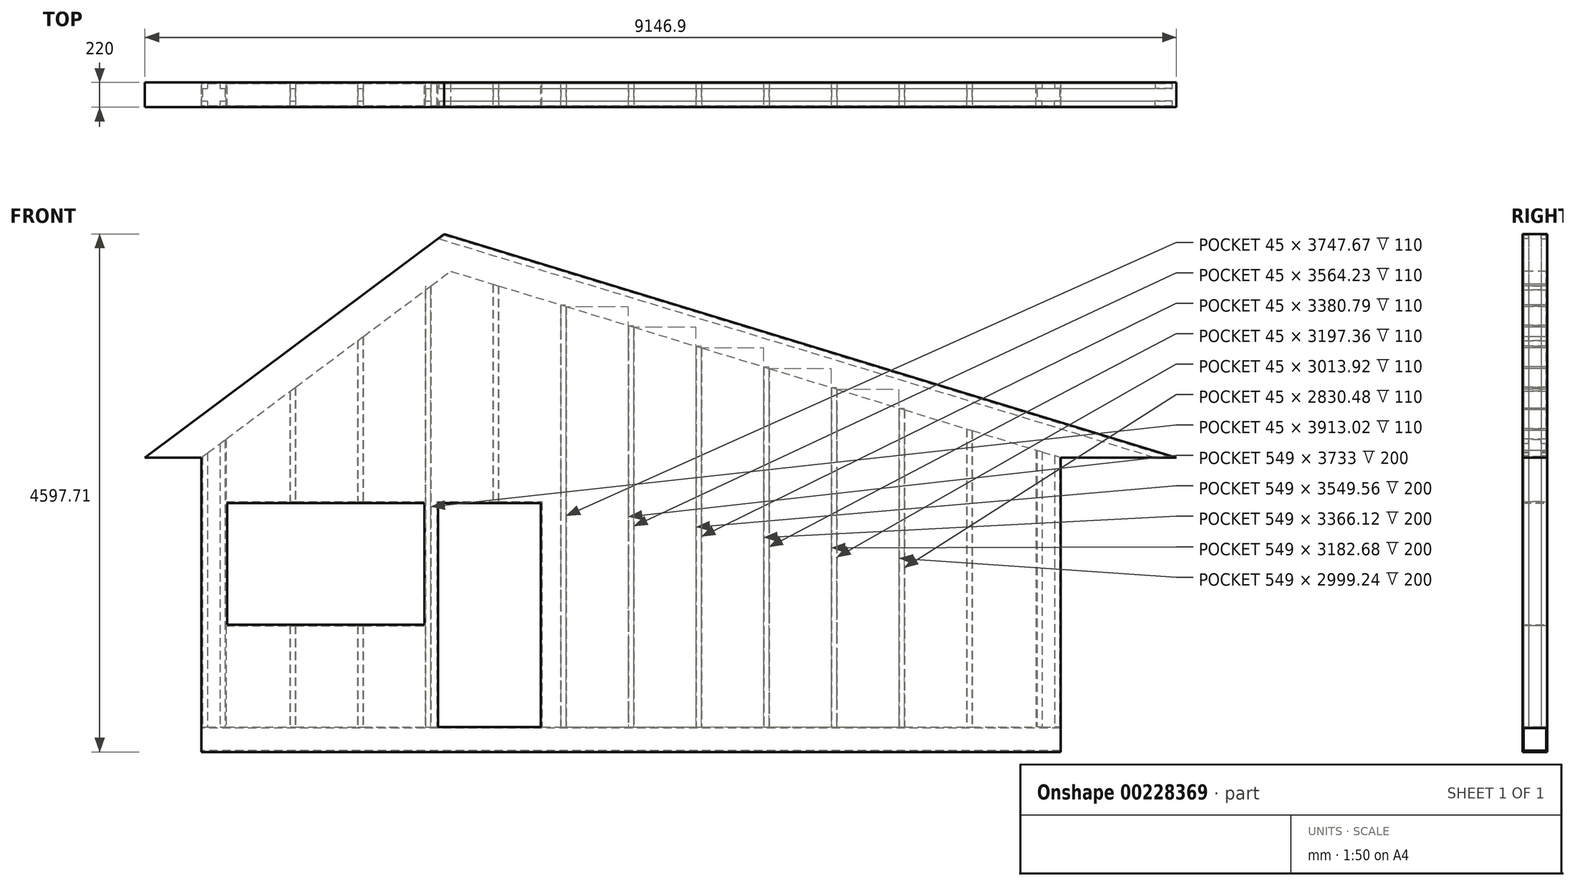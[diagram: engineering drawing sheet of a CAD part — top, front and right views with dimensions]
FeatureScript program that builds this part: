
annotation { "Feature Type Name" : "Feature", "Feature Type Description" : "" }
export const myFeature = defineFeature(function(context is Context, id is Id, definition is map)
    precondition{}
    {
        {
            var Q0;
            Q0=qCreatedBy(makeId("Top.planeOp"),FACE);
            var sketch = newSketch(context, id + "F0", { "sketchPlane" : qUnion([Q0])});
            skLineSegment(sketch, "E0.bottom", {"start": v(0, 0) * mm, "end": v(7600, 0) * mm});
            skLineSegment(sketch, "E0.top", {"start": v(0, -200) * mm, "end": v(7600, -200) * mm});
            skLineSegment(sketch, "E0.left", {"start": v(0, 0) * mm, "end": v(0, -200) * mm});
            skLineSegment(sketch, "E0.right", {"start": v(7600, 0) * mm, "end": v(7600, -200) * mm});
            skLineSegment(sketch, "E1.bottom", {"start": v(-10, 10) * mm, "end": v(7610, 10) * mm});
            skLineSegment(sketch, "E1.top", {"start": v(-10, -210) * mm, "end": v(7610, -210) * mm});
            skLineSegment(sketch, "E1.left", {"start": v(-10, 10) * mm, "end": v(-10, -210) * mm});
            skLineSegment(sketch, "E1.right", {"start": v(7610, 10) * mm, "end": v(7610, -210) * mm});
            skLineSegment(sketch, "E2.bottom", {"start": v(0, 0) * mm, "end": v(45, 0) * mm});
            skLineSegment(sketch, "E2.top", {"start": v(0, -45) * mm, "end": v(45, -45) * mm});
            skLineSegment(sketch, "E2.left", {"start": v(0, 0) * mm, "end": v(0, -45) * mm});
            skLineSegment(sketch, "E2.right", {"start": v(45, 0) * mm, "end": v(45, -45) * mm});
            skLineSegment(sketch, "E3.0.1.0", {"start": v(0, -200) * mm, "end": v(45, -200) * mm});
            skLineSegment(sketch, "E3.0.1.1", {"start": v(0, -155) * mm, "end": v(0, -200) * mm});
            skLineSegment(sketch, "E3.0.1.2", {"start": v(0, -155) * mm, "end": v(45, -155) * mm});
            skLineSegment(sketch, "E3.0.1.3", {"start": v(45, -155) * mm, "end": v(45, -200) * mm});
            skLineSegment(sketch, "E3.1.0.0", {"start": v(155, -45) * mm, "end": v(200, -45) * mm});
            skLineSegment(sketch, "E3.1.0.1", {"start": v(155, 0) * mm, "end": v(155, -45) * mm});
            skLineSegment(sketch, "E3.1.0.2", {"start": v(155, 0) * mm, "end": v(200, 0) * mm});
            skLineSegment(sketch, "E3.1.0.3", {"start": v(200, 0) * mm, "end": v(200, -45) * mm});
            skLineSegment(sketch, "E3.1.1.0", {"start": v(155, -200) * mm, "end": v(200, -200) * mm});
            skLineSegment(sketch, "E3.1.1.1", {"start": v(155, -155) * mm, "end": v(155, -200) * mm});
            skLineSegment(sketch, "E3.1.1.2", {"start": v(155, -155) * mm, "end": v(200, -155) * mm});
            skLineSegment(sketch, "E3.1.1.3", {"start": v(200, -155) * mm, "end": v(200, -200) * mm});
            skLineSegment(sketch, "E3.direction1", {"start": v(0, -45) * mm, "end": v(155, -45) * mm, "construction": true});
            skLineSegment(sketch, "E3.direction2", {"start": v(0, -45) * mm, "end": v(0, -200) * mm, "construction": true});
            skLineSegment(sketch, "E4", {"start": v(200, 0) * mm, "end": v(200, -200) * mm});
            skLineSegment(sketch, "E5", {"start": v(210, 0) * mm, "end": v(210, -200) * mm});
            skLineSegment(sketch, "E6.bottom", {"start": v(777.5, 0) * mm, "end": v(822.5, 0) * mm});
            skLineSegment(sketch, "E6.top", {"start": v(777.5, -45) * mm, "end": v(822.5, -45) * mm});
            skLineSegment(sketch, "E6.left", {"start": v(777.5, 0) * mm, "end": v(777.5, -45) * mm});
            skLineSegment(sketch, "E6.right", {"start": v(822.5, 0) * mm, "end": v(822.5, -45) * mm});
            skLineSegment(sketch, "E7.bottom", {"start": v(777.5, -200) * mm, "end": v(822.5, -200) * mm});
            skLineSegment(sketch, "E7.top", {"start": v(777.5, -155) * mm, "end": v(822.5, -155) * mm});
            skLineSegment(sketch, "E7.left", {"start": v(777.5, -200) * mm, "end": v(777.5, -155) * mm});
            skLineSegment(sketch, "E7.right", {"start": v(822.5, -200) * mm, "end": v(822.5, -155) * mm});
            skLineSegment(sketch, "E8", {"start": v(774.5, 0) * mm, "end": v(774.5, -200) * mm});
            skLineSegment(sketch, "E9", {"start": v(777.5, -45) * mm, "end": v(777.5, -155) * mm});
            skLineSegment(sketch, "E10", {"start": v(822.5, -45) * mm, "end": v(822.5, -155) * mm});
            skLineSegment(sketch, "E11", {"start": v(825.5, 0) * mm, "end": v(825.5, -200) * mm});
            skLineSegment(sketch, "E12", {"start": v(800, -200) * mm, "end": v(800, -155) * mm});
            skLineSegment(sketch, "E13.1.0.0", {"start": v(1400, -200) * mm, "end": v(1400, -155) * mm});
            skLineSegment(sketch, "E13.1.0.1", {"start": v(1377.5, -200) * mm, "end": v(1377.5, -155) * mm});
            skLineSegment(sketch, "E13.1.0.2", {"start": v(1374.5, 0) * mm, "end": v(1374.5, -200) * mm});
            skLineSegment(sketch, "E13.1.0.3", {"start": v(1377.5, -45) * mm, "end": v(1422.5, -45) * mm});
            skLineSegment(sketch, "E13.1.0.4", {"start": v(1377.5, -155) * mm, "end": v(1422.5, -155) * mm});
            skLineSegment(sketch, "E13.1.0.5", {"start": v(1377.5, -200) * mm, "end": v(1422.5, -200) * mm});
            skLineSegment(sketch, "E13.1.0.6", {"start": v(1377.5, 0) * mm, "end": v(1377.5, -45) * mm});
            skLineSegment(sketch, "E13.1.0.7", {"start": v(1422.5, -45) * mm, "end": v(1422.5, -155) * mm});
            skLineSegment(sketch, "E13.1.0.8", {"start": v(1377.5, -45) * mm, "end": v(1377.5, -155) * mm});
            skLineSegment(sketch, "E13.1.0.9", {"start": v(1422.5, -200) * mm, "end": v(1422.5, -155) * mm});
            skLineSegment(sketch, "E13.1.0.10", {"start": v(1377.5, 0) * mm, "end": v(1422.5, 0) * mm});
            skLineSegment(sketch, "E13.1.0.11", {"start": v(1422.5, 0) * mm, "end": v(1422.5, -45) * mm});
            skLineSegment(sketch, "E13.1.0.12", {"start": v(1425.5, 0) * mm, "end": v(1425.5, -200) * mm});
            skLineSegment(sketch, "E13.2.0.0", {"start": v(2000, -200) * mm, "end": v(2000, -155) * mm});
            skLineSegment(sketch, "E13.2.0.1", {"start": v(1977.5, -200) * mm, "end": v(1977.5, -155) * mm});
            skLineSegment(sketch, "E13.2.0.2", {"start": v(1974.5, 0) * mm, "end": v(1974.5, -200) * mm});
            skLineSegment(sketch, "E13.2.0.3", {"start": v(1977.5, -45) * mm, "end": v(2022.5, -45) * mm});
            skLineSegment(sketch, "E13.2.0.4", {"start": v(1977.5, -155) * mm, "end": v(2022.5, -155) * mm});
            skLineSegment(sketch, "E13.2.0.5", {"start": v(1977.5, -200) * mm, "end": v(2022.5, -200) * mm});
            skLineSegment(sketch, "E13.2.0.6", {"start": v(1977.5, 0) * mm, "end": v(1977.5, -45) * mm});
            skLineSegment(sketch, "E13.2.0.7", {"start": v(2022.5, -45) * mm, "end": v(2022.5, -155) * mm});
            skLineSegment(sketch, "E13.2.0.8", {"start": v(1977.5, -45) * mm, "end": v(1977.5, -155) * mm});
            skLineSegment(sketch, "E13.2.0.9", {"start": v(2022.5, -200) * mm, "end": v(2022.5, -155) * mm});
            skLineSegment(sketch, "E13.2.0.10", {"start": v(1977.5, 0) * mm, "end": v(2022.5, 0) * mm});
            skLineSegment(sketch, "E13.2.0.11", {"start": v(2022.5, 0) * mm, "end": v(2022.5, -45) * mm});
            skLineSegment(sketch, "E13.2.0.12", {"start": v(2025.5, 0) * mm, "end": v(2025.5, -200) * mm});
            skLineSegment(sketch, "E13.3.0.0", {"start": v(2600, -200) * mm, "end": v(2600, -155) * mm});
            skLineSegment(sketch, "E13.3.0.1", {"start": v(2577.5, -200) * mm, "end": v(2577.5, -155) * mm});
            skLineSegment(sketch, "E13.3.0.2", {"start": v(2574.5, 0) * mm, "end": v(2574.5, -200) * mm});
            skLineSegment(sketch, "E13.3.0.3", {"start": v(2577.5, -45) * mm, "end": v(2622.5, -45) * mm});
            skLineSegment(sketch, "E13.3.0.4", {"start": v(2577.5, -155) * mm, "end": v(2622.5, -155) * mm});
            skLineSegment(sketch, "E13.3.0.5", {"start": v(2577.5, -200) * mm, "end": v(2622.5, -200) * mm});
            skLineSegment(sketch, "E13.3.0.6", {"start": v(2577.5, 0) * mm, "end": v(2577.5, -45) * mm});
            skLineSegment(sketch, "E13.3.0.7", {"start": v(2622.5, -45) * mm, "end": v(2622.5, -155) * mm});
            skLineSegment(sketch, "E13.3.0.8", {"start": v(2577.5, -45) * mm, "end": v(2577.5, -155) * mm});
            skLineSegment(sketch, "E13.3.0.9", {"start": v(2622.5, -200) * mm, "end": v(2622.5, -155) * mm});
            skLineSegment(sketch, "E13.3.0.10", {"start": v(2577.5, 0) * mm, "end": v(2622.5, 0) * mm});
            skLineSegment(sketch, "E13.3.0.11", {"start": v(2622.5, 0) * mm, "end": v(2622.5, -45) * mm});
            skLineSegment(sketch, "E13.3.0.12", {"start": v(2625.5, 0) * mm, "end": v(2625.5, -200) * mm});
            skLineSegment(sketch, "E13.4.0.0", {"start": v(3200, -200) * mm, "end": v(3200, -155) * mm});
            skLineSegment(sketch, "E13.4.0.1", {"start": v(3177.5, -200) * mm, "end": v(3177.5, -155) * mm});
            skLineSegment(sketch, "E13.4.0.2", {"start": v(3174.5, 0) * mm, "end": v(3174.5, -200) * mm});
            skLineSegment(sketch, "E13.4.0.3", {"start": v(3177.5, -45) * mm, "end": v(3222.5, -45) * mm});
            skLineSegment(sketch, "E13.4.0.4", {"start": v(3177.5, -155) * mm, "end": v(3222.5, -155) * mm});
            skLineSegment(sketch, "E13.4.0.5", {"start": v(3177.5, -200) * mm, "end": v(3222.5, -200) * mm});
            skLineSegment(sketch, "E13.4.0.6", {"start": v(3177.5, 0) * mm, "end": v(3177.5, -45) * mm});
            skLineSegment(sketch, "E13.4.0.7", {"start": v(3222.5, -45) * mm, "end": v(3222.5, -155) * mm});
            skLineSegment(sketch, "E13.4.0.8", {"start": v(3177.5, -45) * mm, "end": v(3177.5, -155) * mm});
            skLineSegment(sketch, "E13.4.0.9", {"start": v(3222.5, -200) * mm, "end": v(3222.5, -155) * mm});
            skLineSegment(sketch, "E13.4.0.10", {"start": v(3177.5, 0) * mm, "end": v(3222.5, 0) * mm});
            skLineSegment(sketch, "E13.4.0.11", {"start": v(3222.5, 0) * mm, "end": v(3222.5, -45) * mm});
            skLineSegment(sketch, "E13.4.0.12", {"start": v(3225.5, 0) * mm, "end": v(3225.5, -200) * mm});
            skLineSegment(sketch, "E13.5.0.0", {"start": v(3800, -200) * mm, "end": v(3800, -155) * mm});
            skLineSegment(sketch, "E13.5.0.1", {"start": v(3777.5, -200) * mm, "end": v(3777.5, -155) * mm});
            skLineSegment(sketch, "E13.5.0.2", {"start": v(3774.5, 0) * mm, "end": v(3774.5, -200) * mm});
            skLineSegment(sketch, "E13.5.0.3", {"start": v(3777.5, -45) * mm, "end": v(3822.5, -45) * mm});
            skLineSegment(sketch, "E13.5.0.4", {"start": v(3777.5, -155) * mm, "end": v(3822.5, -155) * mm});
            skLineSegment(sketch, "E13.5.0.5", {"start": v(3777.5, -200) * mm, "end": v(3822.5, -200) * mm});
            skLineSegment(sketch, "E13.5.0.6", {"start": v(3777.5, 0) * mm, "end": v(3777.5, -45) * mm});
            skLineSegment(sketch, "E13.5.0.7", {"start": v(3822.5, -45) * mm, "end": v(3822.5, -155) * mm});
            skLineSegment(sketch, "E13.5.0.8", {"start": v(3777.5, -45) * mm, "end": v(3777.5, -155) * mm});
            skLineSegment(sketch, "E13.5.0.9", {"start": v(3822.5, -200) * mm, "end": v(3822.5, -155) * mm});
            skLineSegment(sketch, "E13.5.0.10", {"start": v(3777.5, 0) * mm, "end": v(3822.5, 0) * mm});
            skLineSegment(sketch, "E13.5.0.11", {"start": v(3822.5, 0) * mm, "end": v(3822.5, -45) * mm});
            skLineSegment(sketch, "E13.5.0.12", {"start": v(3825.5, 0) * mm, "end": v(3825.5, -200) * mm});
            skLineSegment(sketch, "E13.6.0.0", {"start": v(4400, -200) * mm, "end": v(4400, -155) * mm});
            skLineSegment(sketch, "E13.6.0.1", {"start": v(4377.5, -200) * mm, "end": v(4377.5, -155) * mm});
            skLineSegment(sketch, "E13.6.0.2", {"start": v(4374.5, 0) * mm, "end": v(4374.5, -200) * mm});
            skLineSegment(sketch, "E13.6.0.3", {"start": v(4377.5, -45) * mm, "end": v(4422.5, -45) * mm});
            skLineSegment(sketch, "E13.6.0.4", {"start": v(4377.5, -155) * mm, "end": v(4422.5, -155) * mm});
            skLineSegment(sketch, "E13.6.0.5", {"start": v(4377.5, -200) * mm, "end": v(4422.5, -200) * mm});
            skLineSegment(sketch, "E13.6.0.6", {"start": v(4377.5, 0) * mm, "end": v(4377.5, -45) * mm});
            skLineSegment(sketch, "E13.6.0.7", {"start": v(4422.5, -45) * mm, "end": v(4422.5, -155) * mm});
            skLineSegment(sketch, "E13.6.0.8", {"start": v(4377.5, -45) * mm, "end": v(4377.5, -155) * mm});
            skLineSegment(sketch, "E13.6.0.9", {"start": v(4422.5, -200) * mm, "end": v(4422.5, -155) * mm});
            skLineSegment(sketch, "E13.6.0.10", {"start": v(4377.5, 0) * mm, "end": v(4422.5, 0) * mm});
            skLineSegment(sketch, "E13.6.0.11", {"start": v(4422.5, 0) * mm, "end": v(4422.5, -45) * mm});
            skLineSegment(sketch, "E13.6.0.12", {"start": v(4425.5, 0) * mm, "end": v(4425.5, -200) * mm});
            skLineSegment(sketch, "E13.7.0.0", {"start": v(5000, -200) * mm, "end": v(5000, -155) * mm});
            skLineSegment(sketch, "E13.7.0.1", {"start": v(4977.5, -200) * mm, "end": v(4977.5, -155) * mm});
            skLineSegment(sketch, "E13.7.0.2", {"start": v(4974.5, 0) * mm, "end": v(4974.5, -200) * mm});
            skLineSegment(sketch, "E13.7.0.3", {"start": v(4977.5, -45) * mm, "end": v(5022.5, -45) * mm});
            skLineSegment(sketch, "E13.7.0.4", {"start": v(4977.5, -155) * mm, "end": v(5022.5, -155) * mm});
            skLineSegment(sketch, "E13.7.0.5", {"start": v(4977.5, -200) * mm, "end": v(5022.5, -200) * mm});
            skLineSegment(sketch, "E13.7.0.6", {"start": v(4977.5, 0) * mm, "end": v(4977.5, -45) * mm});
            skLineSegment(sketch, "E13.7.0.7", {"start": v(5022.5, -45) * mm, "end": v(5022.5, -155) * mm});
            skLineSegment(sketch, "E13.7.0.8", {"start": v(4977.5, -45) * mm, "end": v(4977.5, -155) * mm});
            skLineSegment(sketch, "E13.7.0.9", {"start": v(5022.5, -200) * mm, "end": v(5022.5, -155) * mm});
            skLineSegment(sketch, "E13.7.0.10", {"start": v(4977.5, 0) * mm, "end": v(5022.5, 0) * mm});
            skLineSegment(sketch, "E13.7.0.11", {"start": v(5022.5, 0) * mm, "end": v(5022.5, -45) * mm});
            skLineSegment(sketch, "E13.7.0.12", {"start": v(5025.5, 0) * mm, "end": v(5025.5, -200) * mm});
            skLineSegment(sketch, "E13.8.0.0", {"start": v(5600, -200) * mm, "end": v(5600, -155) * mm});
            skLineSegment(sketch, "E13.8.0.1", {"start": v(5577.5, -200) * mm, "end": v(5577.5, -155) * mm});
            skLineSegment(sketch, "E13.8.0.2", {"start": v(5574.5, 0) * mm, "end": v(5574.5, -200) * mm});
            skLineSegment(sketch, "E13.8.0.3", {"start": v(5577.5, -45) * mm, "end": v(5622.5, -45) * mm});
            skLineSegment(sketch, "E13.8.0.4", {"start": v(5577.5, -155) * mm, "end": v(5622.5, -155) * mm});
            skLineSegment(sketch, "E13.8.0.5", {"start": v(5577.5, -200) * mm, "end": v(5622.5, -200) * mm});
            skLineSegment(sketch, "E13.8.0.6", {"start": v(5577.5, 0) * mm, "end": v(5577.5, -45) * mm});
            skLineSegment(sketch, "E13.8.0.7", {"start": v(5622.5, -45) * mm, "end": v(5622.5, -155) * mm});
            skLineSegment(sketch, "E13.8.0.8", {"start": v(5577.5, -45) * mm, "end": v(5577.5, -155) * mm});
            skLineSegment(sketch, "E13.8.0.9", {"start": v(5622.5, -200) * mm, "end": v(5622.5, -155) * mm});
            skLineSegment(sketch, "E13.8.0.10", {"start": v(5577.5, 0) * mm, "end": v(5622.5, 0) * mm});
            skLineSegment(sketch, "E13.8.0.11", {"start": v(5622.5, 0) * mm, "end": v(5622.5, -45) * mm});
            skLineSegment(sketch, "E13.8.0.12", {"start": v(5625.5, 0) * mm, "end": v(5625.5, -200) * mm});
            skLineSegment(sketch, "E13.9.0.0", {"start": v(6200, -200) * mm, "end": v(6200, -155) * mm});
            skLineSegment(sketch, "E13.9.0.1", {"start": v(6177.5, -200) * mm, "end": v(6177.5, -155) * mm});
            skLineSegment(sketch, "E13.9.0.2", {"start": v(6174.5, 0) * mm, "end": v(6174.5, -200) * mm});
            skLineSegment(sketch, "E13.9.0.3", {"start": v(6177.5, -45) * mm, "end": v(6222.5, -45) * mm});
            skLineSegment(sketch, "E13.9.0.4", {"start": v(6177.5, -155) * mm, "end": v(6222.5, -155) * mm});
            skLineSegment(sketch, "E13.9.0.5", {"start": v(6177.5, -200) * mm, "end": v(6222.5, -200) * mm});
            skLineSegment(sketch, "E13.9.0.6", {"start": v(6177.5, 0) * mm, "end": v(6177.5, -45) * mm});
            skLineSegment(sketch, "E13.9.0.7", {"start": v(6222.5, -45) * mm, "end": v(6222.5, -155) * mm});
            skLineSegment(sketch, "E13.9.0.8", {"start": v(6177.5, -45) * mm, "end": v(6177.5, -155) * mm});
            skLineSegment(sketch, "E13.9.0.9", {"start": v(6222.5, -200) * mm, "end": v(6222.5, -155) * mm});
            skLineSegment(sketch, "E13.9.0.10", {"start": v(6177.5, 0) * mm, "end": v(6222.5, 0) * mm});
            skLineSegment(sketch, "E13.9.0.11", {"start": v(6222.5, 0) * mm, "end": v(6222.5, -45) * mm});
            skLineSegment(sketch, "E13.9.0.12", {"start": v(6225.5, 0) * mm, "end": v(6225.5, -200) * mm});
            skLineSegment(sketch, "E13.10.0.0", {"start": v(6800, -200) * mm, "end": v(6800, -155) * mm});
            skLineSegment(sketch, "E13.10.0.1", {"start": v(6777.5, -200) * mm, "end": v(6777.5, -155) * mm});
            skLineSegment(sketch, "E13.10.0.2", {"start": v(6774.5, 0) * mm, "end": v(6774.5, -200) * mm});
            skLineSegment(sketch, "E13.10.0.3", {"start": v(6777.5, -45) * mm, "end": v(6822.5, -45) * mm});
            skLineSegment(sketch, "E13.10.0.4", {"start": v(6777.5, -155) * mm, "end": v(6822.5, -155) * mm});
            skLineSegment(sketch, "E13.10.0.5", {"start": v(6777.5, -200) * mm, "end": v(6822.5, -200) * mm});
            skLineSegment(sketch, "E13.10.0.6", {"start": v(6777.5, 0) * mm, "end": v(6777.5, -45) * mm});
            skLineSegment(sketch, "E13.10.0.7", {"start": v(6822.5, -45) * mm, "end": v(6822.5, -155) * mm});
            skLineSegment(sketch, "E13.10.0.8", {"start": v(6777.5, -45) * mm, "end": v(6777.5, -155) * mm});
            skLineSegment(sketch, "E13.10.0.9", {"start": v(6822.5, -200) * mm, "end": v(6822.5, -155) * mm});
            skLineSegment(sketch, "E13.10.0.10", {"start": v(6777.5, 0) * mm, "end": v(6822.5, 0) * mm});
            skLineSegment(sketch, "E13.10.0.11", {"start": v(6822.5, 0) * mm, "end": v(6822.5, -45) * mm});
            skLineSegment(sketch, "E13.10.0.12", {"start": v(6825.5, 0) * mm, "end": v(6825.5, -200) * mm});
            skLineSegment(sketch, "E13.direction1", {"start": v(777.5, -155) * mm, "end": v(1377.5, -155) * mm, "construction": true});
            skLineSegment(sketch, "E14.bottom", {"start": v(7600, 0) * mm, "end": v(7556, 0) * mm});
            skLineSegment(sketch, "E14.top", {"start": v(7600, -45) * mm, "end": v(7556, -45) * mm});
            skLineSegment(sketch, "E14.left", {"start": v(7600, 0) * mm, "end": v(7600, -45) * mm});
            skLineSegment(sketch, "E14.right", {"start": v(7556, 0) * mm, "end": v(7556, -45) * mm});
            skLineSegment(sketch, "E15.bottom", {"start": v(7600, -200) * mm, "end": v(7555, -200) * mm});
            skLineSegment(sketch, "E15.top", {"start": v(7600, -155) * mm, "end": v(7555, -155) * mm});
            skLineSegment(sketch, "E15.left", {"start": v(7600, -200) * mm, "end": v(7600, -155) * mm});
            skLineSegment(sketch, "E15.right", {"start": v(7555, -200) * mm, "end": v(7555, -155) * mm});
            skLineSegment(sketch, "E16.bottom", {"start": v(7445, -200) * mm, "end": v(7400, -200) * mm});
            skLineSegment(sketch, "E16.top", {"start": v(7445, -155) * mm, "end": v(7400, -155) * mm});
            skLineSegment(sketch, "E16.left", {"start": v(7445, -200) * mm, "end": v(7445, -155) * mm});
            skLineSegment(sketch, "E16.right", {"start": v(7400, -200) * mm, "end": v(7400, -155) * mm});
            skLineSegment(sketch, "E17.bottom", {"start": v(7445, 0) * mm, "end": v(7400, 0) * mm});
            skLineSegment(sketch, "E17.top", {"start": v(7445, -45) * mm, "end": v(7400, -45) * mm});
            skLineSegment(sketch, "E17.left", {"start": v(7445, 0) * mm, "end": v(7445, -45) * mm});
            skLineSegment(sketch, "E17.right", {"start": v(7400, 0) * mm, "end": v(7400, -45) * mm});
            skLineSegment(sketch, "E18", {"start": v(7400, -45) * mm, "end": v(7400, -155) * mm});
            skLineSegment(sketch, "E19", {"start": v(7390, -200) * mm, "end": v(7390, 0) * mm});
            skSolve(sketch);
        }
        {
            var Q0;
            Q0 = qSketchRegion(id + "F0", true);
            var Q1;
            {var subQ4=sQuery(id+"F0.wireOp",EDGE,"E2.top");Q1=makeQuery(id+"F0.imprint","IMPRINT",FACE,{"disambiguationData":[TD([[makeQuery(id+"F0.imprint","IMPRINT",EDGE,{"derivedFrom":subQ4}),1.0]])]});}
            var Q2;
            {var subQ4=sQuery(id+"F0.wireOp",EDGE,"E3.0.1.2");Q2=makeQuery(id+"F0.imprint","IMPRINT",FACE,{"disambiguationData":[TD([[makeQuery(id+"F0.imprint","IMPRINT",EDGE,{"derivedFrom":subQ4}),-1.0]])]});}
            var Q3;
            {var subQ0=sQuery(id+"F0.wireOp",EDGE,"E3.1.1.1");Q3=makeQuery(id+"F0.imprint","IMPRINT",FACE,{"disambiguationData":[TD([[makeQuery(id+"F0.imprint","IMPRINT",EDGE,{"derivedFrom":subQ0}),1.0]])]});}
            var Q4;
            Q4=makeQuery(id+"F0.imprint","IMPRINT",FACE,{"disambiguationData":[TD([[makeQuery(id+"F0.imprint","IMPRINT",EDGE,{"derivedFrom":sQuery(id+"F0.wireOp",EDGE,"E3.1.0.0")}),1.0]])]});
            var Q5;
            {var subQ1=sQuery(id+"F0.wireOp",EDGE,"E3.1.0.3");Q5=makeQuery(id+"F0.imprint","IMPRINT",FACE,{"disambiguationData":[TD([[makeQuery(id+"F0.imprint","IMPRINT",EDGE,{"derivedFrom":subQ1}),1.0]])]});}
            var Q6;
            Q6=makeQuery(id+"F0.imprint","IMPRINT",FACE,{"disambiguationData":[TD([[makeQuery(id+"F0.imprint","IMPRINT",EDGE,{"derivedFrom":sQuery(id+"F0.wireOp",EDGE,"E6.top")}),1.0]])]});
            var Q7;
            {var subQ3=sQuery(id+"F0.wireOp",EDGE,"E6.left");Q7=makeQuery(id+"F0.imprint","IMPRINT",FACE,{"disambiguationData":[TD([[makeQuery(id+"F0.imprint","IMPRINT",EDGE,{"derivedFrom":subQ3}),-1.0]])]});}
            var Q8;
            {var subQ0=sQuery(id+"F0.wireOp",EDGE,"E6.right");Q8=makeQuery(id+"F0.imprint","IMPRINT",FACE,{"disambiguationData":[TD([[makeQuery(id+"F0.imprint","IMPRINT",EDGE,{"derivedFrom":subQ0}),1.0]])]});}
            var Q9;
            {var subQ0=sQuery(id+"F0.wireOp",EDGE,"E7.right");Q9=makeQuery(id+"F0.imprint","IMPRINT",FACE,{"disambiguationData":[TD([[makeQuery(id+"F0.imprint","IMPRINT",EDGE,{"derivedFrom":subQ0}),1.0]])]});}
            var Q10;
            {var subQ0=sQuery(id+"F0.wireOp",EDGE,"E7.left");Q10=makeQuery(id+"F0.imprint","IMPRINT",FACE,{"disambiguationData":[TD([[makeQuery(id+"F0.imprint","IMPRINT",EDGE,{"derivedFrom":subQ0}),-1.0]])]});}
            var Q11;
            Q11=makeQuery(id+"F0.imprint","IMPRINT",FACE,{"disambiguationData":[TD([[makeQuery(id+"F0.imprint","IMPRINT",EDGE,{"derivedFrom":sQuery(id+"F0.wireOp",EDGE,"E13.1.0.3")}),1.0]])]});
            var Q12;
            {var subQ0=sQuery(id+"F0.wireOp",EDGE,"E13.1.0.1");Q12=makeQuery(id+"F0.imprint","IMPRINT",FACE,{"disambiguationData":[TD([[makeQuery(id+"F0.imprint","IMPRINT",EDGE,{"derivedFrom":subQ0}),1.0]])]});}
            var Q13;
            Q13=makeQuery(id+"F0.imprint","IMPRINT",FACE,{"disambiguationData":[TD([[makeQuery(id+"F0.imprint","IMPRINT",EDGE,{"derivedFrom":sQuery(id+"F0.wireOp",EDGE,"E13.1.0.7")}),1.0]])]});
            var Q14;
            {var subQ0=sQuery(id+"F0.wireOp",EDGE,"E13.1.0.0");Q14=makeQuery(id+"F0.imprint","IMPRINT",FACE,{"disambiguationData":[TD([[makeQuery(id+"F0.imprint","IMPRINT",EDGE,{"derivedFrom":subQ0}),-1.0]])]});}
            var Q15;
            {var subQ0=sQuery(id+"F0.wireOp",EDGE,"E13.1.0.0");Q15=makeQuery(id+"F0.imprint","IMPRINT",FACE,{"disambiguationData":[TD([[makeQuery(id+"F0.imprint","IMPRINT",EDGE,{"derivedFrom":subQ0}),1.0]])]});}
            var Q16;
            Q16=makeQuery(id+"F0.imprint","IMPRINT",FACE,{"disambiguationData":[TD([[makeQuery(id+"F0.imprint","IMPRINT",EDGE,{"derivedFrom":sQuery(id+"F0.wireOp",EDGE,"E13.2.0.3")}),1.0]])]});
            var Q17;
            {var subQ0=sQuery(id+"F0.wireOp",EDGE,"E13.2.0.0");Q17=makeQuery(id+"F0.imprint","IMPRINT",FACE,{"disambiguationData":[TD([[makeQuery(id+"F0.imprint","IMPRINT",EDGE,{"derivedFrom":subQ0}),-1.0]])]});}
            var Q18;
            {var subQ0=sQuery(id+"F0.wireOp",EDGE,"E13.2.0.0");Q18=makeQuery(id+"F0.imprint","IMPRINT",FACE,{"disambiguationData":[TD([[makeQuery(id+"F0.imprint","IMPRINT",EDGE,{"derivedFrom":subQ0}),1.0]])]});}
            var Q19;
            {var subQ1=sQuery(id+"F0.wireOp",EDGE,"E13.2.0.1");Q19=makeQuery(id+"F0.imprint","IMPRINT",FACE,{"disambiguationData":[TD([[makeQuery(id+"F0.imprint","IMPRINT",EDGE,{"derivedFrom":subQ1}),1.0]])]});}
            var Q20;
            Q20=makeQuery(id+"F0.imprint","IMPRINT",FACE,{"disambiguationData":[TD([[makeQuery(id+"F0.imprint","IMPRINT",EDGE,{"derivedFrom":sQuery(id+"F0.wireOp",EDGE,"E13.2.0.7")}),1.0]])]});
            var Q21;
            Q21=makeQuery(id+"F0.imprint","IMPRINT",FACE,{"disambiguationData":[TD([[makeQuery(id+"F0.imprint","IMPRINT",EDGE,{"derivedFrom":sQuery(id+"F0.wireOp",EDGE,"E13.3.0.3")}),1.0]])]});
            var Q22;
            Q22=makeQuery(id+"F0.imprint","IMPRINT",FACE,{"disambiguationData":[TD([[makeQuery(id+"F0.imprint","IMPRINT",EDGE,{"derivedFrom":sQuery(id+"F0.wireOp",EDGE,"E13.3.0.7")}),1.0]])]});
            var Q23;
            {var subQ1=sQuery(id+"F0.wireOp",EDGE,"E13.3.0.1");Q23=makeQuery(id+"F0.imprint","IMPRINT",FACE,{"disambiguationData":[TD([[makeQuery(id+"F0.imprint","IMPRINT",EDGE,{"derivedFrom":subQ1}),1.0]])]});}
            var Q24;
            {var subQ0=sQuery(id+"F0.wireOp",EDGE,"E13.3.0.0");Q24=makeQuery(id+"F0.imprint","IMPRINT",FACE,{"disambiguationData":[TD([[makeQuery(id+"F0.imprint","IMPRINT",EDGE,{"derivedFrom":subQ0}),1.0]])]});}
            var Q25;
            {var subQ0=sQuery(id+"F0.wireOp",EDGE,"E13.3.0.0");Q25=makeQuery(id+"F0.imprint","IMPRINT",FACE,{"disambiguationData":[TD([[makeQuery(id+"F0.imprint","IMPRINT",EDGE,{"derivedFrom":subQ0}),-1.0]])]});}
            var Q26;
            Q26=makeQuery(id+"F0.imprint","IMPRINT",FACE,{"disambiguationData":[TD([[makeQuery(id+"F0.imprint","IMPRINT",EDGE,{"derivedFrom":sQuery(id+"F0.wireOp",EDGE,"E13.4.0.3")}),1.0]])]});
            var Q27;
            {var subQ1=sQuery(id+"F0.wireOp",EDGE,"E13.4.0.1");Q27=makeQuery(id+"F0.imprint","IMPRINT",FACE,{"disambiguationData":[TD([[makeQuery(id+"F0.imprint","IMPRINT",EDGE,{"derivedFrom":subQ1}),1.0]])]});}
            var Q28;
            Q28=makeQuery(id+"F0.imprint","IMPRINT",FACE,{"disambiguationData":[TD([[makeQuery(id+"F0.imprint","IMPRINT",EDGE,{"derivedFrom":sQuery(id+"F0.wireOp",EDGE,"E13.4.0.7")}),1.0]])]});
            var Q29;
            {var subQ0=sQuery(id+"F0.wireOp",EDGE,"E13.4.0.0");Q29=makeQuery(id+"F0.imprint","IMPRINT",FACE,{"disambiguationData":[TD([[makeQuery(id+"F0.imprint","IMPRINT",EDGE,{"derivedFrom":subQ0}),-1.0]])]});}
            var Q30;
            {var subQ0=sQuery(id+"F0.wireOp",EDGE,"E13.4.0.0");Q30=makeQuery(id+"F0.imprint","IMPRINT",FACE,{"disambiguationData":[TD([[makeQuery(id+"F0.imprint","IMPRINT",EDGE,{"derivedFrom":subQ0}),1.0]])]});}
            var Q31;
            Q31=makeQuery(id+"F0.imprint","IMPRINT",FACE,{"disambiguationData":[TD([[makeQuery(id+"F0.imprint","IMPRINT",EDGE,{"derivedFrom":sQuery(id+"F0.wireOp",EDGE,"E13.5.0.3")}),1.0]])]});
            var Q32;
            {var subQ1=sQuery(id+"F0.wireOp",EDGE,"E13.5.0.1");Q32=makeQuery(id+"F0.imprint","IMPRINT",FACE,{"disambiguationData":[TD([[makeQuery(id+"F0.imprint","IMPRINT",EDGE,{"derivedFrom":subQ1}),1.0]])]});}
            var Q33;
            Q33=makeQuery(id+"F0.imprint","IMPRINT",FACE,{"disambiguationData":[TD([[makeQuery(id+"F0.imprint","IMPRINT",EDGE,{"derivedFrom":sQuery(id+"F0.wireOp",EDGE,"E13.5.0.7")}),1.0]])]});
            var Q34;
            {var subQ0=sQuery(id+"F0.wireOp",EDGE,"E13.5.0.0");Q34=makeQuery(id+"F0.imprint","IMPRINT",FACE,{"disambiguationData":[TD([[makeQuery(id+"F0.imprint","IMPRINT",EDGE,{"derivedFrom":subQ0}),-1.0]])]});}
            var Q35;
            {var subQ0=sQuery(id+"F0.wireOp",EDGE,"E13.5.0.0");Q35=makeQuery(id+"F0.imprint","IMPRINT",FACE,{"disambiguationData":[TD([[makeQuery(id+"F0.imprint","IMPRINT",EDGE,{"derivedFrom":subQ0}),1.0]])]});}
            var Q36;
            Q36=makeQuery(id+"F0.imprint","IMPRINT",FACE,{"disambiguationData":[TD([[makeQuery(id+"F0.imprint","IMPRINT",EDGE,{"derivedFrom":sQuery(id+"F0.wireOp",EDGE,"E13.6.0.3")}),1.0]])]});
            var Q37;
            {var subQ1=sQuery(id+"F0.wireOp",EDGE,"E13.6.0.1");Q37=makeQuery(id+"F0.imprint","IMPRINT",FACE,{"disambiguationData":[TD([[makeQuery(id+"F0.imprint","IMPRINT",EDGE,{"derivedFrom":subQ1}),1.0]])]});}
            var Q38;
            Q38=makeQuery(id+"F0.imprint","IMPRINT",FACE,{"disambiguationData":[TD([[makeQuery(id+"F0.imprint","IMPRINT",EDGE,{"derivedFrom":sQuery(id+"F0.wireOp",EDGE,"E13.6.0.7")}),1.0]])]});
            var Q39;
            {var subQ0=sQuery(id+"F0.wireOp",EDGE,"E13.6.0.0");Q39=makeQuery(id+"F0.imprint","IMPRINT",FACE,{"disambiguationData":[TD([[makeQuery(id+"F0.imprint","IMPRINT",EDGE,{"derivedFrom":subQ0}),-1.0]])]});}
            var Q40;
            {var subQ0=sQuery(id+"F0.wireOp",EDGE,"E13.6.0.0");Q40=makeQuery(id+"F0.imprint","IMPRINT",FACE,{"disambiguationData":[TD([[makeQuery(id+"F0.imprint","IMPRINT",EDGE,{"derivedFrom":subQ0}),1.0]])]});}
            var Q41;
            Q41=makeQuery(id+"F0.imprint","IMPRINT",FACE,{"disambiguationData":[TD([[makeQuery(id+"F0.imprint","IMPRINT",EDGE,{"derivedFrom":sQuery(id+"F0.wireOp",EDGE,"E13.7.0.3")}),1.0]])]});
            var Q42;
            Q42=makeQuery(id+"F0.imprint","IMPRINT",FACE,{"disambiguationData":[TD([[makeQuery(id+"F0.imprint","IMPRINT",EDGE,{"derivedFrom":sQuery(id+"F0.wireOp",EDGE,"E13.7.0.7")}),1.0]])]});
            var Q43;
            {var subQ1=sQuery(id+"F0.wireOp",EDGE,"E13.7.0.1");Q43=makeQuery(id+"F0.imprint","IMPRINT",FACE,{"disambiguationData":[TD([[makeQuery(id+"F0.imprint","IMPRINT",EDGE,{"derivedFrom":subQ1}),1.0]])]});}
            var Q44;
            {var subQ0=sQuery(id+"F0.wireOp",EDGE,"E13.7.0.0");Q44=makeQuery(id+"F0.imprint","IMPRINT",FACE,{"disambiguationData":[TD([[makeQuery(id+"F0.imprint","IMPRINT",EDGE,{"derivedFrom":subQ0}),-1.0]])]});}
            var Q45;
            {var subQ0=sQuery(id+"F0.wireOp",EDGE,"E13.7.0.0");Q45=makeQuery(id+"F0.imprint","IMPRINT",FACE,{"disambiguationData":[TD([[makeQuery(id+"F0.imprint","IMPRINT",EDGE,{"derivedFrom":subQ0}),1.0]])]});}
            var Q46;
            Q46=makeQuery(id+"F0.imprint","IMPRINT",FACE,{"disambiguationData":[TD([[makeQuery(id+"F0.imprint","IMPRINT",EDGE,{"derivedFrom":sQuery(id+"F0.wireOp",EDGE,"E13.8.0.3")}),1.0]])]});
            var Q47;
            {var subQ1=sQuery(id+"F0.wireOp",EDGE,"E13.8.0.1");Q47=makeQuery(id+"F0.imprint","IMPRINT",FACE,{"disambiguationData":[TD([[makeQuery(id+"F0.imprint","IMPRINT",EDGE,{"derivedFrom":subQ1}),1.0]])]});}
            var Q48;
            Q48=makeQuery(id+"F0.imprint","IMPRINT",FACE,{"disambiguationData":[TD([[makeQuery(id+"F0.imprint","IMPRINT",EDGE,{"derivedFrom":sQuery(id+"F0.wireOp",EDGE,"E13.8.0.7")}),1.0]])]});
            var Q49;
            {var subQ0=sQuery(id+"F0.wireOp",EDGE,"E13.8.0.0");Q49=makeQuery(id+"F0.imprint","IMPRINT",FACE,{"disambiguationData":[TD([[makeQuery(id+"F0.imprint","IMPRINT",EDGE,{"derivedFrom":subQ0}),-1.0]])]});}
            var Q50;
            {var subQ0=sQuery(id+"F0.wireOp",EDGE,"E13.8.0.0");Q50=makeQuery(id+"F0.imprint","IMPRINT",FACE,{"disambiguationData":[TD([[makeQuery(id+"F0.imprint","IMPRINT",EDGE,{"derivedFrom":subQ0}),1.0]])]});}
            var Q51;
            Q51=makeQuery(id+"F0.imprint","IMPRINT",FACE,{"disambiguationData":[TD([[makeQuery(id+"F0.imprint","IMPRINT",EDGE,{"derivedFrom":sQuery(id+"F0.wireOp",EDGE,"E13.9.0.3")}),1.0]])]});
            var Q52;
            {var subQ1=sQuery(id+"F0.wireOp",EDGE,"E13.9.0.1");Q52=makeQuery(id+"F0.imprint","IMPRINT",FACE,{"disambiguationData":[TD([[makeQuery(id+"F0.imprint","IMPRINT",EDGE,{"derivedFrom":subQ1}),1.0]])]});}
            var Q53;
            Q53=makeQuery(id+"F0.imprint","IMPRINT",FACE,{"disambiguationData":[TD([[makeQuery(id+"F0.imprint","IMPRINT",EDGE,{"derivedFrom":sQuery(id+"F0.wireOp",EDGE,"E13.9.0.7")}),1.0]])]});
            var Q54;
            {var subQ0=sQuery(id+"F0.wireOp",EDGE,"E13.9.0.0");Q54=makeQuery(id+"F0.imprint","IMPRINT",FACE,{"disambiguationData":[TD([[makeQuery(id+"F0.imprint","IMPRINT",EDGE,{"derivedFrom":subQ0}),-1.0]])]});}
            var Q55;
            {var subQ0=sQuery(id+"F0.wireOp",EDGE,"E13.9.0.0");Q55=makeQuery(id+"F0.imprint","IMPRINT",FACE,{"disambiguationData":[TD([[makeQuery(id+"F0.imprint","IMPRINT",EDGE,{"derivedFrom":subQ0}),1.0]])]});}
            var Q56;
            Q56=makeQuery(id+"F0.imprint","IMPRINT",FACE,{"disambiguationData":[TD([[makeQuery(id+"F0.imprint","IMPRINT",EDGE,{"derivedFrom":sQuery(id+"F0.wireOp",EDGE,"E13.10.0.3")}),1.0]])]});
            var Q57;
            {var subQ1=sQuery(id+"F0.wireOp",EDGE,"E13.10.0.1");Q57=makeQuery(id+"F0.imprint","IMPRINT",FACE,{"disambiguationData":[TD([[makeQuery(id+"F0.imprint","IMPRINT",EDGE,{"derivedFrom":subQ1}),1.0]])]});}
            var Q58;
            Q58=makeQuery(id+"F0.imprint","IMPRINT",FACE,{"disambiguationData":[TD([[makeQuery(id+"F0.imprint","IMPRINT",EDGE,{"derivedFrom":sQuery(id+"F0.wireOp",EDGE,"E13.10.0.7")}),1.0]])]});
            var Q59;
            {var subQ0=sQuery(id+"F0.wireOp",EDGE,"E13.10.0.0");Q59=makeQuery(id+"F0.imprint","IMPRINT",FACE,{"disambiguationData":[TD([[makeQuery(id+"F0.imprint","IMPRINT",EDGE,{"derivedFrom":subQ0}),1.0]])]});}
            var Q60;
            {var subQ0=sQuery(id+"F0.wireOp",EDGE,"E13.10.0.0");Q60=makeQuery(id+"F0.imprint","IMPRINT",FACE,{"disambiguationData":[TD([[makeQuery(id+"F0.imprint","IMPRINT",EDGE,{"derivedFrom":subQ0}),-1.0]])]});}
            var Q61;
            Q61=makeQuery(id+"F0.imprint","IMPRINT",FACE,{"disambiguationData":[TD([[makeQuery(id+"F0.imprint","IMPRINT",EDGE,{"derivedFrom":sQuery(id+"F0.wireOp",EDGE,"E17.top")}),-1.0]])]});
            var Q62;
            {var subQ0=sQuery(id+"F0.wireOp",EDGE,"E16.right");Q62=makeQuery(id+"F0.imprint","IMPRINT",FACE,{"disambiguationData":[TD([[makeQuery(id+"F0.imprint","IMPRINT",EDGE,{"derivedFrom":subQ0}),1.0]])]});}
            var Q63;
            Q63=makeQuery(id+"F0.imprint","IMPRINT",FACE,{"disambiguationData":[TD([[makeQuery(id+"F0.imprint","IMPRINT",EDGE,{"derivedFrom":sQuery(id+"F0.wireOp",EDGE,"E16.top")}),1.0]])]});
            var Q64;
            {var subQ4=sQuery(id+"F0.wireOp",EDGE,"E15.top");Q64=makeQuery(id+"F0.imprint","IMPRINT",FACE,{"disambiguationData":[TD([[makeQuery(id+"F0.imprint","IMPRINT",EDGE,{"derivedFrom":subQ4}),1.0]])]});}
            var Q65;
            {var subQ4=sQuery(id+"F0.wireOp",EDGE,"E14.top");Q65=makeQuery(id+"F0.imprint","IMPRINT",FACE,{"disambiguationData":[TD([[makeQuery(id+"F0.imprint","IMPRINT",EDGE,{"derivedFrom":subQ4}),-1.0]])]});}
            extrude(context, id + "F1", {"entities" : qUnion([Q0, Q1, Q2, Q3, Q4, Q5, Q6, Q7, Q8, Q9, Q10, Q11, Q12, Q13, Q14, Q15, Q16, Q17, Q18, Q19, Q20, Q21, Q22, Q23, Q24, Q25, Q26, Q27, Q28, Q29, Q30, Q31, Q32, Q33, Q34, Q35, Q36, Q37, Q38, Q39, Q40, Q41, Q42, Q43, Q44, Q45, Q46, Q47, Q48, Q49, Q50, Q51, Q52, Q53, Q54, Q55, Q56, Q57, Q58, Q59, Q60, Q61, Q62, Q63, Q64, Q65]), "depth" : 4100 * mm, "offsetDistance" : 25 * mm});
        }
        {
            var Q0;
            Q0=makeQuery(id+"F1.opExtrude","SWEPT_FACE",FACE,{"disambiguationData":[OSD([sQuery(id+"F0.wireOp",EDGE,"E1.bottom")])]});
            var sketch = newSketch(context, id + "F2", { "sketchPlane" : qUnion([Q0])});
            skLineSegment(sketch, "E20", {"start": v(0, 0) * mm, "end": v(10, 2392.52) * mm});
            skLineSegment(sketch, "E21", {"start": v(10, 2392.52) * mm, "end": v(-2200.68, 4046.32) * mm});
            skLineSegment(sketch, "E22", {"start": v(-2200.68, 4046.32) * mm, "end": v(-7610, 2392.52) * mm});
            skLineSegment(sketch, "E23", {"start": v(-7610, 2392.52) * mm, "end": v(-7610, 0) * mm});
            skLineSegment(sketch, "E24", {"start": v(-7610, 0) * mm, "end": v(10, 0) * mm});
            skPoint(sketch, "E25", {"position": v(0, 2400) * mm});
            skLineSegment(sketch, "E26.bottom", {"start": v(-210, 2000) * mm, "end": v(-1977.5, 2000) * mm});
            skLineSegment(sketch, "E26.top", {"start": v(-210, 900) * mm, "end": v(-1977.5, 900) * mm});
            skLineSegment(sketch, "E26.left", {"start": v(-210, 2000) * mm, "end": v(-210, 900) * mm});
            skLineSegment(sketch, "E26.right", {"start": v(-1977.5, 2000) * mm, "end": v(-1977.5, 900) * mm});
            skLineSegment(sketch, "E27.bottom", {"start": v(-2079.5, 2000) * mm, "end": v(-3009.5, 2000) * mm});
            skLineSegment(sketch, "E27.top", {"start": v(-2079.5, 0) * mm, "end": v(-3009.5, 0) * mm});
            skLineSegment(sketch, "E27.left", {"start": v(-2079.5, 2000) * mm, "end": v(-2079.5, 0) * mm});
            skLineSegment(sketch, "E27.right", {"start": v(-3009.5, 2000) * mm, "end": v(-3009.5, 0) * mm});
            skLineSegment(sketch, "E28.bottom", {"start": v(-1967.5, 1990) * mm, "end": v(-220, 1990) * mm});
            skLineSegment(sketch, "E28.top", {"start": v(-1967.5, 910) * mm, "end": v(-220, 910) * mm});
            skLineSegment(sketch, "E28.left", {"start": v(-1967.5, 1990) * mm, "end": v(-1967.5, 910) * mm});
            skLineSegment(sketch, "E28.right", {"start": v(-220, 1990) * mm, "end": v(-220, 910) * mm});
            skLineSegment(sketch, "E29", {"start": v(-2999.5, 0) * mm, "end": v(-2999.5, 1990) * mm});
            skLineSegment(sketch, "E30", {"start": v(-2999.5, 1990) * mm, "end": v(-2089.5, 1990) * mm});
            skLineSegment(sketch, "E31", {"start": v(-2089.5, 1990) * mm, "end": v(-2089.5, 0) * mm});
            skSolve(sketch);
        }
        {
            var Q0;
            {var subQ0=sQuery(id+"F2.wireOp",EDGE,"E29");Q0=makeQuery(id+"F2.imprint","IMPRINT",FACE,{"disambiguationData":[TD([[makeQuery(id+"F2.imprint","IMPRINT",EDGE,{"derivedFrom":subQ0}),-1.0]])]});}
            var Q1;
            Q1=makeQuery(id+"F2.imprint","IMPRINT",FACE,{"disambiguationData":[TD([[makeQuery(id+"F2.imprint","IMPRINT",EDGE,{"derivedFrom":sQuery(id+"F2.wireOp",EDGE,"E28.bottom")}),-1.0]])]});
            var Q2;
            {var subQ4=sQuery(id+"F2.wireOp",EDGE,"E21");Q2=makeQuery(id+"F2.imprint","IMPRINT",FACE,{"disambiguationData":[TD([[makeQuery(id+"F2.imprint","IMPRINT",EDGE,{"derivedFrom":subQ4}),-1.0]])]});}
            extrude(context, id + "F3", {"entities" : qUnion([Q0, Q1, Q2]), "operationType" : NewBodyOperationType.REMOVE, "oppositeDirection" : true, "depth" : 220 * mm, "offsetDistance" : 25 * mm});
        }
        {
            var Q0;
            Q0=makeQuery(id+"F2.imprint","IMPRINT",FACE,{"disambiguationData":[TD([[makeQuery(id+"F2.imprint","IMPRINT",EDGE,{"derivedFrom":sQuery(id+"F2.wireOp",EDGE,"E27.bottom")}),1.0]])]});
            var Q1;
            Q1=makeQuery(id+"F2.imprint","IMPRINT",FACE,{"disambiguationData":[TD([[makeQuery(id+"F2.imprint","IMPRINT",EDGE,{"derivedFrom":sQuery(id+"F2.wireOp",EDGE,"E26.bottom")}),1.0]])]});
            extrude(context, id + "F4", {"entities" : qUnion([Q0, Q1]), "operationType" : NewBodyOperationType.ADD, "oppositeDirection" : true, "depth" : 220 * mm, "offsetDistance" : 25 * mm});
        }
        {
            var Q0;
            Q0=makeQuery(id+"F1.opExtrude","SWEPT_FACE",FACE,{"disambiguationData":[OSD([sQuery(id+"F0.wireOp",EDGE,"E1.left")])]});
            var sketch = newSketch(context, id + "F5", { "sketchPlane" : qUnion([Q0])});
            skLineSegment(sketch, "E32.bottom", {"start": v(-10, 0) * mm, "end": v(210, 0) * mm});
            skLineSegment(sketch, "E32.top", {"start": v(-10, -220) * mm, "end": v(210, -220) * mm});
            skLineSegment(sketch, "E32.left", {"start": v(-10, 0) * mm, "end": v(-10, -220) * mm});
            skLineSegment(sketch, "E32.right", {"start": v(210, 0) * mm, "end": v(210, -220) * mm});
            skLineSegment(sketch, "E33.bottom", {"start": v(0, -10) * mm, "end": v(200, -10) * mm});
            skLineSegment(sketch, "E33.top", {"start": v(0, -210) * mm, "end": v(200, -210) * mm});
            skLineSegment(sketch, "E33.left", {"start": v(0, -10) * mm, "end": v(0, -210) * mm});
            skLineSegment(sketch, "E33.right", {"start": v(200, -10) * mm, "end": v(200, -210) * mm});
            skLineSegment(sketch, "E34.bottom", {"start": v(0, -10) * mm, "end": v(45, -10) * mm});
            skLineSegment(sketch, "E34.top", {"start": v(0, -55) * mm, "end": v(45, -55) * mm});
            skLineSegment(sketch, "E34.left", {"start": v(0, -10) * mm, "end": v(0, -55) * mm});
            skLineSegment(sketch, "E34.right", {"start": v(45, -10) * mm, "end": v(45, -55) * mm});
            skLineSegment(sketch, "E35.bottom", {"start": v(0, -210) * mm, "end": v(45, -210) * mm});
            skLineSegment(sketch, "E35.top", {"start": v(0, -165) * mm, "end": v(45, -165) * mm});
            skLineSegment(sketch, "E35.left", {"start": v(0, -210) * mm, "end": v(0, -165) * mm});
            skLineSegment(sketch, "E35.right", {"start": v(45, -210) * mm, "end": v(45, -165) * mm});
            skLineSegment(sketch, "E36.bottom", {"start": v(200, -210) * mm, "end": v(155, -210) * mm});
            skLineSegment(sketch, "E36.top", {"start": v(200, -165) * mm, "end": v(155, -165) * mm});
            skLineSegment(sketch, "E36.left", {"start": v(200, -210) * mm, "end": v(200, -165) * mm});
            skLineSegment(sketch, "E36.right", {"start": v(155, -210) * mm, "end": v(155, -165) * mm});
            skLineSegment(sketch, "E37.bottom", {"start": v(200, -10) * mm, "end": v(155, -10) * mm});
            skLineSegment(sketch, "E37.top", {"start": v(200, -55) * mm, "end": v(155, -55) * mm});
            skLineSegment(sketch, "E37.left", {"start": v(200, -10) * mm, "end": v(200, -55) * mm});
            skLineSegment(sketch, "E37.right", {"start": v(155, -10) * mm, "end": v(155, -55) * mm});
            skSolve(sketch);
        }
        {
            var Q0;
            Q0 = qSketchRegion(id + "F5", true);
            var Q1;
            Q1=makeQuery(id+"F5.imprint","IMPRINT",FACE,{"disambiguationData":[TD([[makeQuery(id+"F5.imprint","IMPRINT",EDGE,{"derivedFrom":sQuery(id+"F5.wireOp",EDGE,"E34.bottom")}),-1.0]])]});
            var Q2;
            Q2=makeQuery(id+"F5.imprint","IMPRINT",FACE,{"disambiguationData":[TD([[makeQuery(id+"F5.imprint","IMPRINT",EDGE,{"derivedFrom":sQuery(id+"F5.wireOp",EDGE,"E35.bottom")}),1.0]])]});
            var Q3;
            Q3=makeQuery(id+"F5.imprint","IMPRINT",FACE,{"disambiguationData":[TD([[makeQuery(id+"F5.imprint","IMPRINT",EDGE,{"derivedFrom":sQuery(id+"F5.wireOp",EDGE,"E36.bottom")}),-1.0]])]});
            var Q4;
            Q4=makeQuery(id+"F5.imprint","IMPRINT",FACE,{"disambiguationData":[TD([[makeQuery(id+"F5.imprint","IMPRINT",EDGE,{"derivedFrom":sQuery(id+"F5.wireOp",EDGE,"E37.bottom")}),1.0]])]});
            extrude(context, id + "F6", {"entities" : qUnion([Q0, Q1, Q2, Q3, Q4]), "operationType" : NewBodyOperationType.ADD, "oppositeDirection" : true, "depth" : 7620 * mm, "offsetDistance" : 25 * mm});
        }
        {
            var Q0;
            Q0=makeQuery(id+"F6.boolean.opBoolean","MERGE",FACE,{"derivedFrom":[makeQuery(id+"F1.opExtrude","SWEPT_FACE",FACE,{"disambiguationData":[OSD([sQuery(id+"F0.wireOp",EDGE,"E1.top")])]}),makeQuery(id+"F6.opExtrude","SWEPT_FACE",FACE,{"disambiguationData":[OSD([sQuery(id+"F5.wireOp",EDGE,"E32.right")])]})]});
            var sketch = newSketch(context, id + "F7", { "sketchPlane" : qUnion([Q0])});
            skLineSegment(sketch, "E38", {"start": v(-10, 2392.52) * mm, "end": v(-510.81, 2392.52) * mm});
            skLineSegment(sketch, "E39", {"start": v(-510.81, 2392.52) * mm, "end": v(2142.84, 4377.7) * mm});
            skLineSegment(sketch, "E40", {"start": v(2142.84, 4377.7) * mm, "end": v(8636.1, 2392.52) * mm});
            skLineSegment(sketch, "E41", {"start": v(8636.1, 2392.52) * mm, "end": v(7610, 2392.52) * mm});
            skLineSegment(sketch, "E42", {"start": v(7610, 2392.52) * mm, "end": v(2200.68, 4046.32) * mm});
            skLineSegment(sketch, "E43", {"start": v(2200.68, 4046.32) * mm, "end": v(-10, 2392.52) * mm});
            skLineSegment(sketch, "E44", {"start": v(2200.68, 4046.32) * mm, "end": v(2142.84, 4377.7) * mm});
            skLineSegment(sketch, "E45", {"start": v(-10, 2392.52) * mm, "end": v(-331.1, 2152.3) * mm});
            skLineSegment(sketch, "E46", {"start": v(-331.1, 2152.3) * mm, "end": v(-510.81, 2392.52) * mm});
            skLineSegment(sketch, "E47", {"start": v(7610, 2392.52) * mm, "end": v(8548.38, 2105.63) * mm});
            skLineSegment(sketch, "E48", {"start": v(8548.38, 2105.63) * mm, "end": v(8636.1, 2392.52) * mm});
            skSolve(sketch);
        }
        {
            var Q0;
            Q0 = qSketchRegion(id + "F7", true);
            extrude(context, id + "F8", {"entities" : qUnion([Q0]), "operationType" : NewBodyOperationType.ADD, "oppositeDirection" : true, "depth" : 220 * mm, "offsetDistance" : 25 * mm});
        }
        {
            var Q0;
            Q0=makeQuery(id+"F8.opExtrude","SWEPT_FACE",FACE,{"disambiguationData":[OSD([sQuery(id+"F7.wireOp",EDGE,"E46")])]});
            var sketch = newSketch(context, id + "F9", { "sketchPlane" : qUnion([Q0])});
            skLineSegment(sketch, "E49.bottom", {"start": v(0, 2211.76) * mm, "end": v(200, 2211.76) * mm});
            skLineSegment(sketch, "E49.top", {"start": v(0, 1931.76) * mm, "end": v(200, 1931.76) * mm});
            skLineSegment(sketch, "E49.left", {"start": v(0, 2211.76) * mm, "end": v(0, 1931.76) * mm});
            skLineSegment(sketch, "E49.right", {"start": v(200, 2211.76) * mm, "end": v(200, 1931.76) * mm});
            skLineSegment(sketch, "E50.bottom", {"start": v(0, 2211.76) * mm, "end": v(45, 2211.76) * mm});
            skLineSegment(sketch, "E50.top", {"start": v(0, 2166.76) * mm, "end": v(45, 2166.76) * mm});
            skLineSegment(sketch, "E50.left", {"start": v(0, 2211.76) * mm, "end": v(0, 2166.76) * mm});
            skLineSegment(sketch, "E50.right", {"start": v(45, 2211.76) * mm, "end": v(45, 2166.76) * mm});
            skLineSegment(sketch, "E51.bottom", {"start": v(200, 2211.76) * mm, "end": v(155, 2211.76) * mm});
            skLineSegment(sketch, "E51.top", {"start": v(200, 2166.76) * mm, "end": v(155, 2166.76) * mm});
            skLineSegment(sketch, "E51.left", {"start": v(200, 2211.76) * mm, "end": v(200, 2166.76) * mm});
            skLineSegment(sketch, "E51.right", {"start": v(155, 2211.76) * mm, "end": v(155, 2166.76) * mm});
            skLineSegment(sketch, "E52.bottom", {"start": v(200, 1931.76) * mm, "end": v(155, 1931.76) * mm});
            skLineSegment(sketch, "E52.top", {"start": v(200, 1976.76) * mm, "end": v(155, 1976.76) * mm});
            skLineSegment(sketch, "E52.left", {"start": v(200, 1931.76) * mm, "end": v(200, 1976.76) * mm});
            skLineSegment(sketch, "E52.right", {"start": v(155, 1931.76) * mm, "end": v(155, 1976.76) * mm});
            skLineSegment(sketch, "E53.bottom", {"start": v(0, 1931.76) * mm, "end": v(45, 1931.76) * mm});
            skLineSegment(sketch, "E53.top", {"start": v(0, 1976.76) * mm, "end": v(45, 1976.76) * mm});
            skLineSegment(sketch, "E53.left", {"start": v(0, 1931.76) * mm, "end": v(0, 1976.76) * mm});
            skLineSegment(sketch, "E53.right", {"start": v(45, 1931.76) * mm, "end": v(45, 1976.76) * mm});
            skSolve(sketch);
        }
        {
            var Q0;
            Q0=makeQuery(id+"F9.imprint","IMPRINT",FACE,{"disambiguationData":[TD([[makeQuery(id+"F9.imprint","IMPRINT",EDGE,{"derivedFrom":sQuery(id+"F9.wireOp",EDGE,"E49.bottom")}),-1.0]])]});
            var Q1;
            Q1=makeQuery(id+"F8.opExtrude","SWEPT_FACE",FACE,{"disambiguationData":[OSD([sQuery(id+"F7.wireOp",EDGE,"E40")])]});
            extrude(context, id + "F10", {"entities" : qUnion([Q0]), "operationType" : NewBodyOperationType.ADD, "endBound" : BoundingType.UP_TO_SURFACE, "oppositeDirection" : true, "depth" : 25 * mm, "endBoundEntityFace" : qUnion([Q1]), "hasOffset" : true, "offsetDistance" : 10 * mm});
        }
        {
            var Q0;
            Q0=makeQuery(id+"F8.opExtrude","SWEPT_FACE",FACE,{"disambiguationData":[OSD([sQuery(id+"F7.wireOp",EDGE,"E48")])]});
            var sketch = newSketch(context, id + "F11", { "sketchPlane" : qUnion([Q0])});
            skLineSegment(sketch, "E54.bottom", {"start": v(-200, 4802.93) * mm, "end": v(0, 4802.93) * mm});
            skLineSegment(sketch, "E54.top", {"start": v(-200, 4522.93) * mm, "end": v(0, 4522.93) * mm});
            skLineSegment(sketch, "E54.left", {"start": v(-200, 4802.93) * mm, "end": v(-200, 4522.93) * mm});
            skLineSegment(sketch, "E54.right", {"start": v(0, 4802.93) * mm, "end": v(0, 4522.93) * mm});
            skLineSegment(sketch, "E55.bottom", {"start": v(-200, 4802.93) * mm, "end": v(-155, 4802.93) * mm});
            skLineSegment(sketch, "E55.top", {"start": v(-200, 4757.93) * mm, "end": v(-155, 4757.93) * mm});
            skLineSegment(sketch, "E55.left", {"start": v(-200, 4802.93) * mm, "end": v(-200, 4757.93) * mm});
            skLineSegment(sketch, "E55.right", {"start": v(-155, 4802.93) * mm, "end": v(-155, 4757.93) * mm});
            skLineSegment(sketch, "E56.bottom", {"start": v(0, 4802.93) * mm, "end": v(-45, 4802.93) * mm});
            skLineSegment(sketch, "E56.top", {"start": v(0, 4757.93) * mm, "end": v(-45, 4757.93) * mm});
            skLineSegment(sketch, "E56.left", {"start": v(0, 4802.93) * mm, "end": v(0, 4757.93) * mm});
            skLineSegment(sketch, "E56.right", {"start": v(-45, 4802.93) * mm, "end": v(-45, 4757.93) * mm});
            skLineSegment(sketch, "E57.bottom", {"start": v(-200, 4522.93) * mm, "end": v(-155, 4522.93) * mm});
            skLineSegment(sketch, "E57.top", {"start": v(-200, 4567.93) * mm, "end": v(-155, 4567.93) * mm});
            skLineSegment(sketch, "E57.left", {"start": v(-200, 4522.93) * mm, "end": v(-200, 4567.93) * mm});
            skLineSegment(sketch, "E57.right", {"start": v(-155, 4522.93) * mm, "end": v(-155, 4567.93) * mm});
            skLineSegment(sketch, "E58.bottom", {"start": v(0, 4522.93) * mm, "end": v(-45, 4522.93) * mm});
            skLineSegment(sketch, "E58.top", {"start": v(0, 4567.93) * mm, "end": v(-45, 4567.93) * mm});
            skLineSegment(sketch, "E58.left", {"start": v(0, 4522.93) * mm, "end": v(0, 4567.93) * mm});
            skLineSegment(sketch, "E58.right", {"start": v(-45, 4522.93) * mm, "end": v(-45, 4567.93) * mm});
            skSolve(sketch);
        }
        {
            var Q0;
            Q0=makeQuery(id+"F11.imprint","IMPRINT",FACE,{"disambiguationData":[TD([[makeQuery(id+"F11.imprint","IMPRINT",EDGE,{"derivedFrom":sQuery(id+"F11.wireOp",EDGE,"E54.bottom")}),-1.0]])]});
            var Q1;
            Q1=makeQuery(id+"F8.opExtrude","SWEPT_FACE",FACE,{"disambiguationData":[OSD([sQuery(id+"F7.wireOp",EDGE,"E39")])]});
            extrude(context, id + "F12", {"entities" : qUnion([Q0]), "operationType" : NewBodyOperationType.REMOVE, "endBound" : BoundingType.UP_TO_SURFACE, "oppositeDirection" : true, "depth" : 25 * mm, "endBoundEntityFace" : qUnion([Q1]), "hasOffset" : true, "offsetDistance" : 10 * mm});
        }
        {
            var Q0;
            Q0=makeQuery(id+"F8.opExtrude","CAP_FACE",FACE,{"disambiguationData":[OSD([sQuery(id+"F7.wireOp",EDGE,"E39"),sQuery(id+"F7.wireOp",EDGE,"E40"),sQuery(id+"F7.wireOp",EDGE,"E42"),sQuery(id+"F7.wireOp",EDGE,"E43"),sQuery(id+"F7.wireOp",EDGE,"E45"),sQuery(id+"F7.wireOp",EDGE,"E46"),sQuery(id+"F7.wireOp",EDGE,"E47"),sQuery(id+"F7.wireOp",EDGE,"E48")])],"isStart":true});
            var sketch = newSketch(context, id + "F13", { "sketchPlane" : qUnion([Q0])});
            skLineSegment(sketch, "E59", {"start": v(8636.1, 2392.52) * mm, "end": v(-510.81, 2392.52) * mm});
            skSolve(sketch);
        }
        {
            var Q0;
            {var subQ1=makeQuery(id+"F8.opExtrude","CAP_EDGE",EDGE,{"disambiguationData":[OSD([sQuery(id+"F7.wireOp",EDGE,"E46")])],"isStart":true});Q0=makeQuery(id+"F13.imprint","IMPRINT",FACE,{"disambiguationData":[TD([[makeQuery(id+"F13.imprint","IMPRINT",EDGE,{"derivedFrom":subQ1}),-1.0]])]});}
            var Q1;
            {var subQ1=makeQuery(id+"F8.opExtrude","CAP_EDGE",EDGE,{"disambiguationData":[OSD([sQuery(id+"F7.wireOp",EDGE,"E48")])],"isStart":true});Q1=makeQuery(id+"F13.imprint","IMPRINT",FACE,{"disambiguationData":[TD([[makeQuery(id+"F13.imprint","IMPRINT",EDGE,{"derivedFrom":subQ1}),1.0]])]});}
            extrude(context, id + "F14", {"entities" : qUnion([Q0, Q1]), "operationType" : NewBodyOperationType.REMOVE, "oppositeDirection" : true, "depth" : 220 * mm, "offsetDistance" : 25 * mm});
        }
    });
